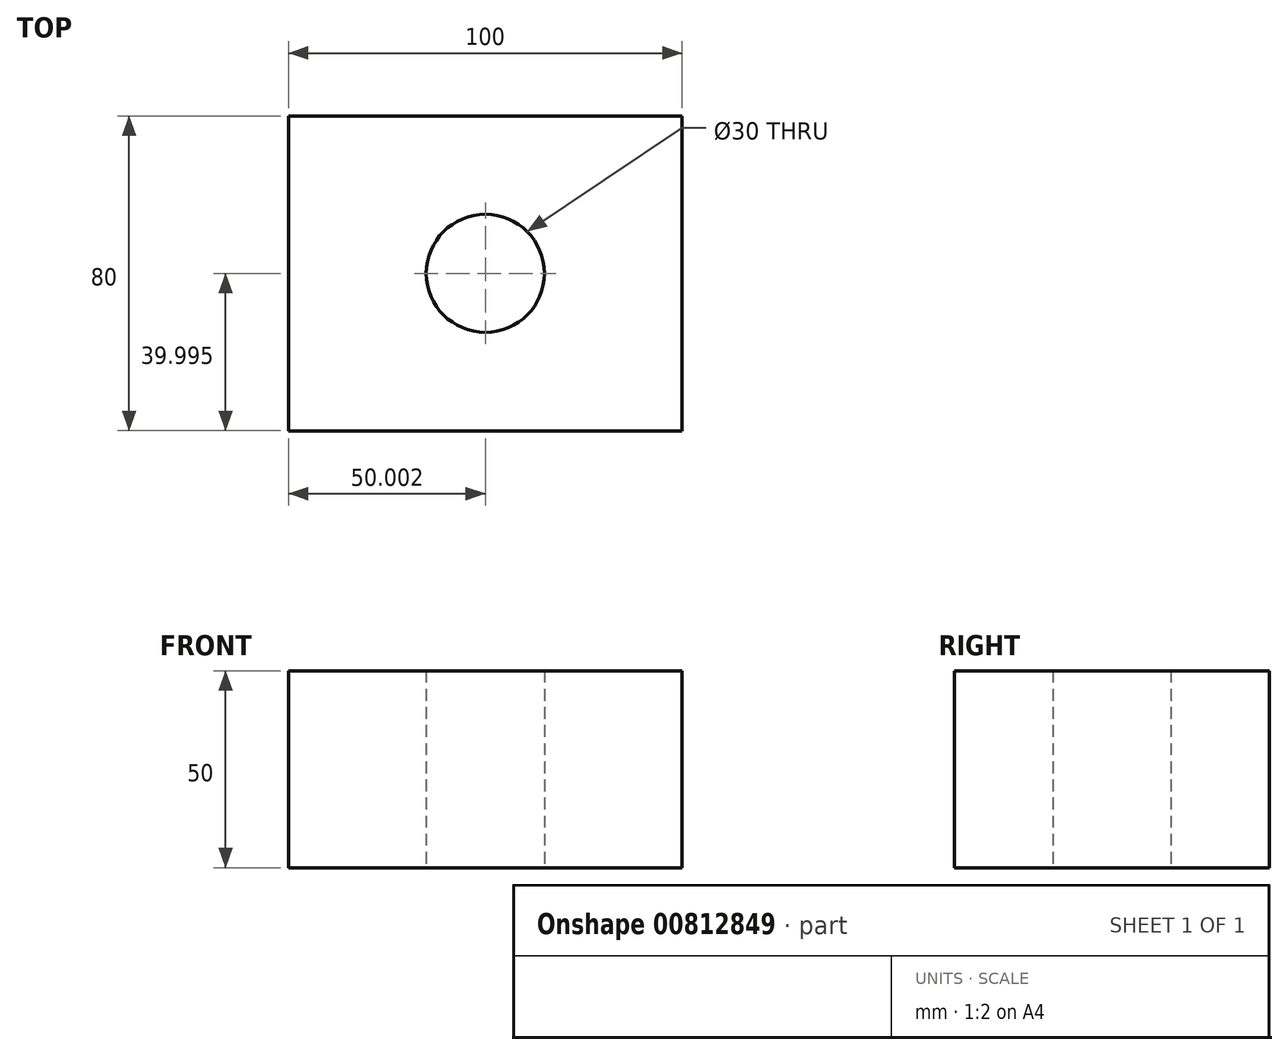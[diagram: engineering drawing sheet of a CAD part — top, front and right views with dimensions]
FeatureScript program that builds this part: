
annotation { "Feature Type Name" : "Feature", "Feature Type Description" : "" }
export const myFeature = defineFeature(function(context is Context, id is Id, definition is map)
    precondition{}
    {
        {
            var Q0;
            Q0=qCreatedBy(makeId("Top.planeOp"),FACE);
            var sketch = newSketch(context, id + "F0", { "sketchPlane" : qUnion([Q0])});
            skLineSegment(sketch, "E0.bottom", {"start": v(-101.8, 22.95) * mm, "end": v(-1.8, 22.95) * mm});
            skLineSegment(sketch, "E0.top", {"start": v(-101.8, -57.05) * mm, "end": v(-1.8, -57.05) * mm});
            skLineSegment(sketch, "E0.left", {"start": v(-101.8, 22.95) * mm, "end": v(-101.8, -57.05) * mm});
            skLineSegment(sketch, "E0.right", {"start": v(-1.8, 22.95) * mm, "end": v(-1.8, -57.05) * mm});
            skCircle(sketch, "E1", {"center": v(-51.8, -17.05) * mm, "radius": 15 * mm});
            skSolve(sketch);
        }
        {
            var Q0;
            Q0=makeQuery(id+"F0.imprint","IMPRINT",FACE,{"disambiguationData":[TD([[makeQuery(id+"F0.imprint","IMPRINT",EDGE,{"derivedFrom":sQuery(id+"F0.wireOp",EDGE,"E0.bottom")}),-1.0]])]});
            extrude(context, id + "F1", {"entities" : qUnion([Q0]), "depth" : 50 * mm, "offsetDistance" : 25 * mm});
        }
    });
